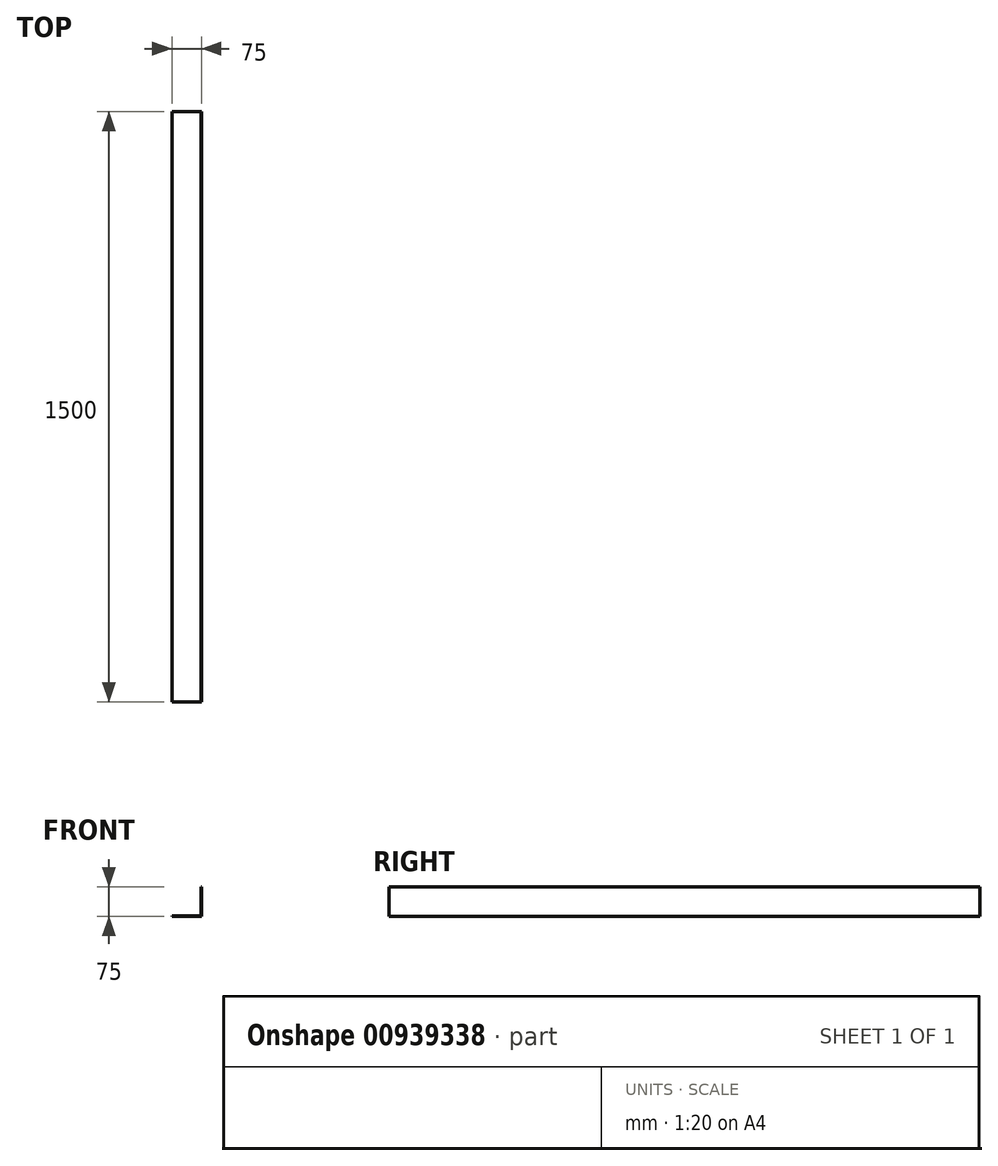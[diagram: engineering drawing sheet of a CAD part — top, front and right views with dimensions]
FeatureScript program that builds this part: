
annotation { "Feature Type Name" : "Feature", "Feature Type Description" : "" }
export const myFeature = defineFeature(function(context is Context, id is Id, definition is map)
    precondition{}
    {
        {
            var Q0;
            Q0=qCreatedBy(makeId("Front.planeOp"),FACE);
            var sketch = newSketch(context, id + "F0", { "sketchPlane" : qUnion([Q0])});
            skLineSegment(sketch, "E0", {"start": v(-37.5, -37.5) * mm, "end": v(37.5, -37.5) * mm});
            skLineSegment(sketch, "E1", {"start": v(37.5, -37.5) * mm, "end": v(37.5, 37.5) * mm});
            skLineSegment(sketch, "E2", {"start": v(-37.5, -37.5) * mm, "end": v(-37.5, -36) * mm});
            skLineSegment(sketch, "E3", {"start": v(-37.5, -36) * mm, "end": v(36, -36) * mm});
            skLineSegment(sketch, "E4", {"start": v(36, -36) * mm, "end": v(36, 37.5) * mm});
            skLineSegment(sketch, "E5", {"start": v(36, 37.5) * mm, "end": v(37.5, 37.5) * mm});
            skSolve(sketch);
        }
        {
            var Q0;
            Q0 = qSketchRegion(id + "F0", true);
            extrude(context, id + "F1", {"entities" : qUnion([Q0]), "depth" : 1500 * mm, "offsetDistance" : 25 * mm});
        }
    });
